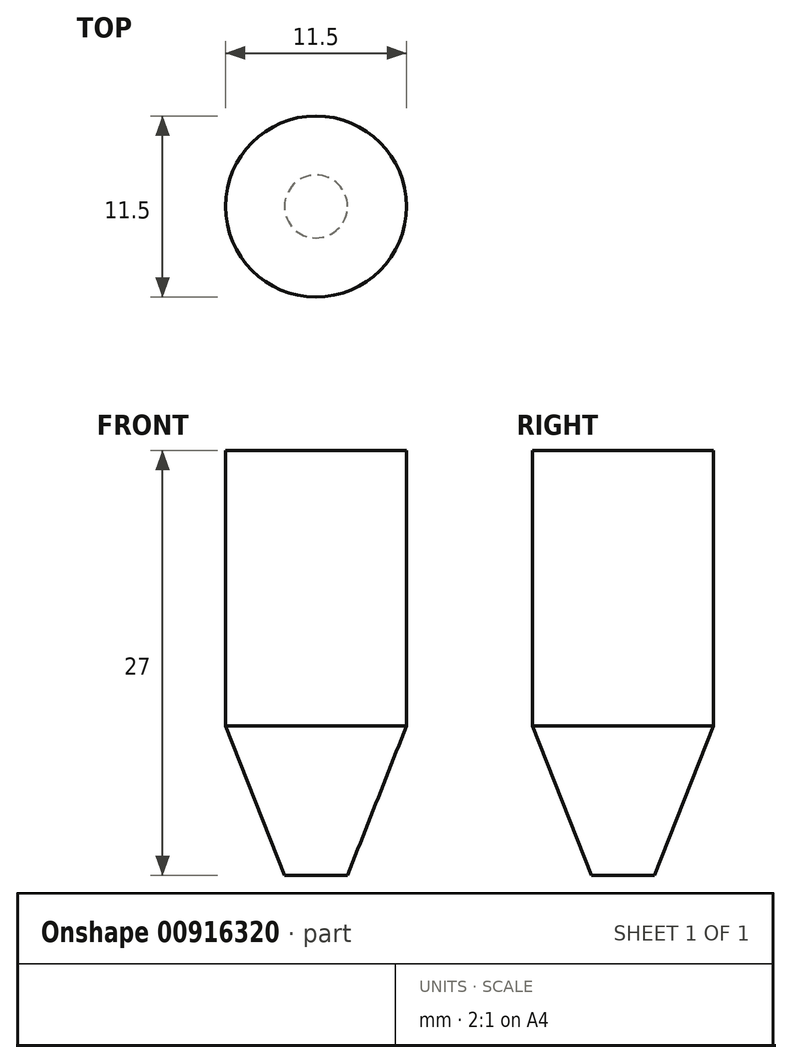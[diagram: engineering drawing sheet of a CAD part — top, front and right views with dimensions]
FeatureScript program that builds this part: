
annotation { "Feature Type Name" : "Feature", "Feature Type Description" : "" }
export const myFeature = defineFeature(function(context is Context, id is Id, definition is map)
    precondition{}
    {
        {
            var Q0;
            Q0=qCreatedBy(makeId("Front.planeOp"),FACE);
            var sketch = newSketch(context, id + "F0", { "sketchPlane" : qUnion([Q0])});
            skLineSegment(sketch, "E0", {"start": v(0, 0) * mm, "end": v(2, 0) * mm});
            skLineSegment(sketch, "E1", {"start": v(2, 0) * mm, "end": v(5.75, 9.5) * mm});
            skLineSegment(sketch, "E2", {"start": v(5.75, 9.5) * mm, "end": v(5.75, 27) * mm});
            skLineSegment(sketch, "E3", {"start": v(5.75, 27) * mm, "end": v(0, 27) * mm});
            skLineSegment(sketch, "E4", {"start": v(0, 27) * mm, "end": v(0, 0) * mm});
            skSolve(sketch);
        }
        {
            var Q0;
            Q0=makeQuery(id+"F0.imprint","IMPRINT",FACE,{"disambiguationData":[TD([[makeQuery(id+"F0.imprint","IMPRINT",EDGE,{"derivedFrom":sQuery(id+"F0.wireOp",EDGE,"E0")}),1.0]])]});
            var Q1;
            Q1=sQuery(id+"F0.wireOp",EDGE,"E4");
            revolve(context, id + "F1", {"surfaceOperationType" : NewSurfaceOperationType.NEW, "entities" : qUnion([Q0]), "axis" : qUnion([Q1]), "revolveType" : RevolveType.FULL});
        }
    });
